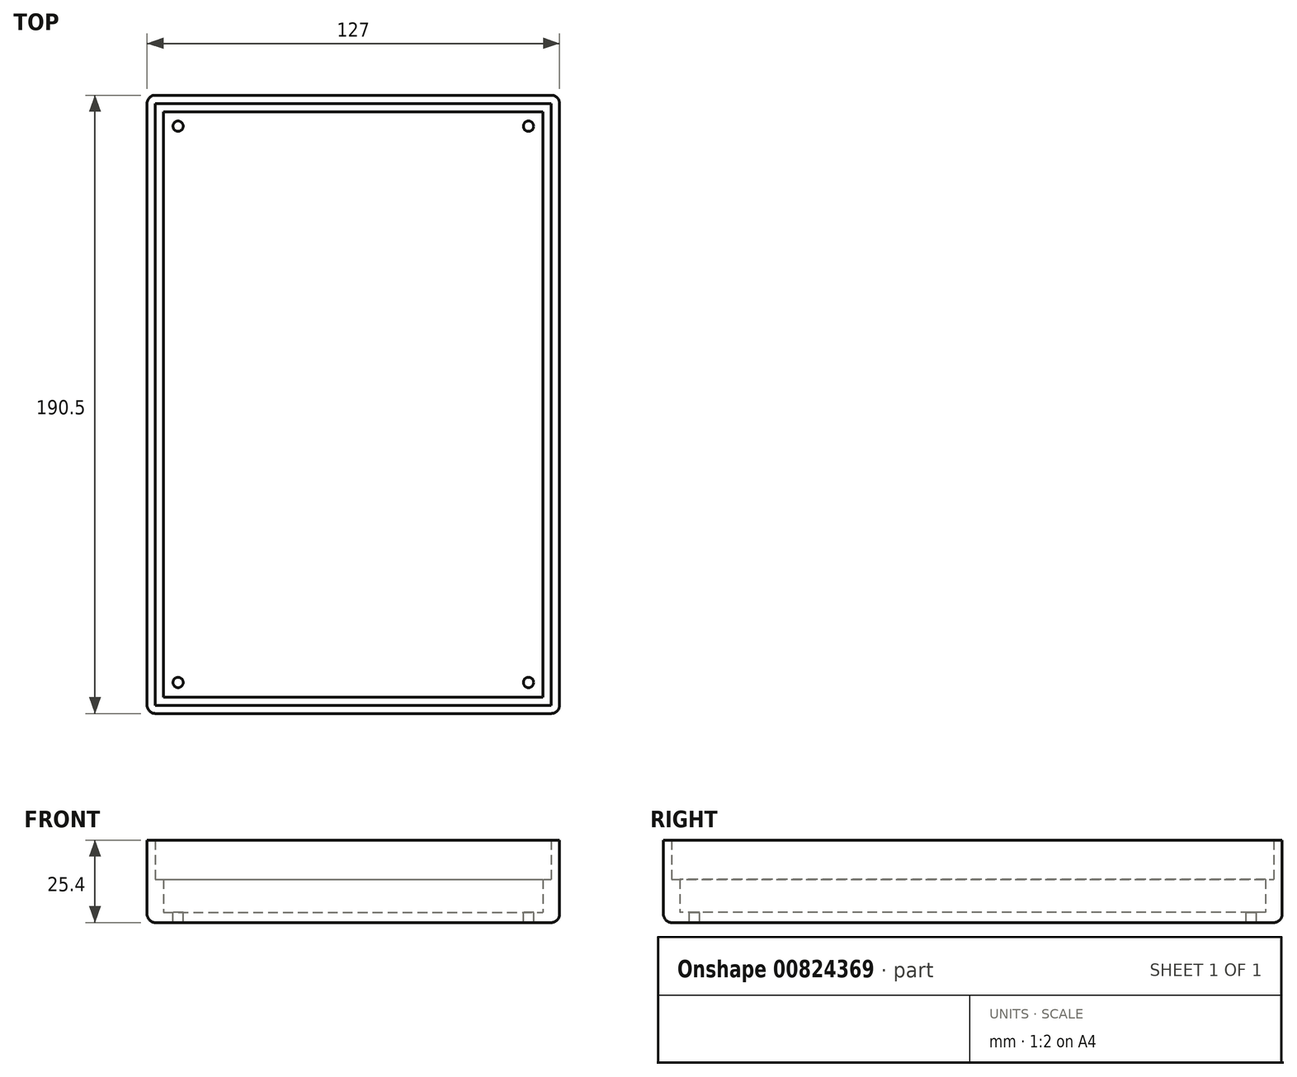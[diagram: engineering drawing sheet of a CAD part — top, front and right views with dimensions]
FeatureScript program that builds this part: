
annotation { "Feature Type Name" : "Feature", "Feature Type Description" : "" }
export const myFeature = defineFeature(function(context is Context, id is Id, definition is map)
    precondition{}
    {
        {
            var Q0;
            Q0=qCreatedBy(makeId("Top.planeOp"),FACE);
            var sketch = newSketch(context, id + "F0", { "sketchPlane" : qUnion([Q0])});
            skLineSegment(sketch, "E0.bottom", {"start": v(-60.96, 92.7) * mm, "end": v(60.96, 92.7) * mm});
            skLineSegment(sketch, "E0.top", {"start": v(-60.96, -92.7) * mm, "end": v(60.96, -92.7) * mm});
            skLineSegment(sketch, "E0.left", {"start": v(-60.96, 92.7) * mm, "end": v(-60.96, -92.7) * mm});
            skLineSegment(sketch, "E0.right", {"start": v(60.96, 92.7) * mm, "end": v(60.96, -92.7) * mm});
            skLineSegment(sketch, "E1.bottom", {"start": v(-63.5, 95.25) * mm, "end": v(63.5, 95.25) * mm});
            skLineSegment(sketch, "E1.top", {"start": v(-63.5, -95.25) * mm, "end": v(63.5, -95.25) * mm});
            skLineSegment(sketch, "E1.left", {"start": v(-63.5, 95.25) * mm, "end": v(-63.5, -95.25) * mm});
            skLineSegment(sketch, "E1.right", {"start": v(63.5, 95.25) * mm, "end": v(63.5, -95.25) * mm});
            skSolve(sketch);
        }
        {
            var Q0;
            Q0=makeQuery(id+"F0.imprint","IMPRINT",FACE,{"disambiguationData":[TD([[makeQuery(id+"F0.imprint","IMPRINT",EDGE,{"derivedFrom":sQuery(id+"F0.wireOp",EDGE,"E0.bottom")}),1.0]])]});
            extrude(context, id + "F1", {"entities" : qUnion([Q0]), "depth" : 25.4 * mm, "offsetDistance" : 25.4 * mm});
        }
        {
            var Q0;
            Q0=makeQuery(id+"F1.opExtrude","SWEPT_FACE",FACE,{"disambiguationData":[OSD([sQuery(id+"F0.wireOp",EDGE,"E0.bottom")])]});
            var sketch = newSketch(context, id + "F2", { "sketchPlane" : qUnion([Q0])});
            skLineSegment(sketch, "E2", {"start": v(-60.96, 3.18) * mm, "end": v(60.96, 3.18) * mm});
            skSolve(sketch);
        }
        {
            var Q0;
            {var subQ0=sQuery(id+"F2.wireOp",EDGE,"E2");Q0=makeQuery(id+"F2.imprint","IMPRINT",FACE,{"disambiguationData":[TD([[makeQuery(id+"F2.imprint","IMPRINT",EDGE,{"derivedFrom":subQ0}),-1.0]])]});}
            extrude(context, id + "F3", {"entities" : qUnion([Q0]), "operationType" : NewBodyOperationType.ADD, "depth" : 185.42 * mm, "offsetDistance" : 25.4 * mm});
        }
        {
            var Q0;
            Q0=makeQuery(id+"F3.opExtrude","SWEPT_FACE",FACE,{"disambiguationData":[OSD([sQuery(id+"F2.wireOp",EDGE,"E2")])]});
            var sketch = newSketch(context, id + "F4", { "sketchPlane" : qUnion([Q0])});
            skLineSegment(sketch, "E3.bottom", {"start": v(-58.42, 90.17) * mm, "end": v(58.42, 90.17) * mm});
            skLineSegment(sketch, "E3.top", {"start": v(-58.42, -90.17) * mm, "end": v(58.42, -90.17) * mm});
            skLineSegment(sketch, "E3.left", {"start": v(-58.42, 90.17) * mm, "end": v(-58.42, -90.17) * mm});
            skLineSegment(sketch, "E3.right", {"start": v(58.42, 90.17) * mm, "end": v(58.42, -90.17) * mm});
            skSolve(sketch);
        }
        {
            var Q0;
            Q0=makeQuery(id+"F4.imprint","IMPRINT",FACE,{"disambiguationData":[TD([[makeQuery(id+"F4.imprint","IMPRINT",EDGE,{"derivedFrom":sQuery(id+"F4.wireOp",EDGE,"E3.bottom")}),1.0]])]});
            extrude(context, id + "F5", {"entities" : qUnion([Q0]), "operationType" : NewBodyOperationType.ADD, "depth" : 10.16 * mm, "offsetDistance" : 25.4 * mm});
        }
        {
            var Q0;
            Q0=makeQuery(id+"F3.opExtrude","SWEPT_FACE",FACE,{"disambiguationData":[OSD([sQuery(id+"F2.wireOp",EDGE,"E2")])]});
            var sketch = newSketch(context, id + "F6", { "sketchPlane" : qUnion([Q0])});
            skLineSegment(sketch, "E4.bottom", {"start": v(-53.95, 85.7) * mm, "end": v(53.95, 85.7) * mm, "construction": true});
            skLineSegment(sketch, "E4.top", {"start": v(-53.95, -85.7) * mm, "end": v(53.95, -85.7) * mm, "construction": true});
            skLineSegment(sketch, "E4.left", {"start": v(-53.95, 85.7) * mm, "end": v(-53.95, -85.7) * mm, "construction": true});
            skLineSegment(sketch, "E4.right", {"start": v(53.95, 85.7) * mm, "end": v(53.95, -85.7) * mm, "construction": true});
            skCircle(sketch, "E5", {"center": v(-53.95, 85.7) * mm, "radius": 1.59 * mm});
            skCircle(sketch, "E6", {"center": v(53.95, 85.7) * mm, "radius": 1.59 * mm});
            skCircle(sketch, "E7", {"center": v(-53.95, -85.7) * mm, "radius": 1.59 * mm});
            skCircle(sketch, "E8", {"center": v(53.95, -85.7) * mm, "radius": 1.59 * mm});
            skSolve(sketch);
        }
        {
            var Q0;
            Q0=makeQuery(id+"F6.imprint","IMPRINT",FACE,{"disambiguationData":[TD([[makeQuery(id+"F6.imprint","IMPRINT",EDGE,{"derivedFrom":sQuery(id+"F6.wireOp",EDGE,"E5")}),1.0]])]});
            var Q1;
            Q1=makeQuery(id+"F6.imprint","IMPRINT",FACE,{"disambiguationData":[TD([[makeQuery(id+"F6.imprint","IMPRINT",EDGE,{"derivedFrom":sQuery(id+"F6.wireOp",EDGE,"E6")}),1.0]])]});
            var Q2;
            Q2=makeQuery(id+"F6.imprint","IMPRINT",FACE,{"disambiguationData":[TD([[makeQuery(id+"F6.imprint","IMPRINT",EDGE,{"derivedFrom":sQuery(id+"F6.wireOp",EDGE,"E7")}),1.0]])]});
            var Q3;
            Q3=makeQuery(id+"F6.imprint","IMPRINT",FACE,{"disambiguationData":[TD([[makeQuery(id+"F6.imprint","IMPRINT",EDGE,{"derivedFrom":sQuery(id+"F6.wireOp",EDGE,"E8")}),1.0]])]});
            extrude(context, id + "F7", {"entities" : qUnion([Q0, Q1, Q2, Q3]), "operationType" : NewBodyOperationType.REMOVE, "oppositeDirection" : true, "depth" : 25.4 * mm, "offsetDistance" : 25.4 * mm});
        }
        {
            var Q0;
            Q0=makeQuery(id+"F1.opExtrude","SWEPT_EDGE",EDGE,{"disambiguationData":[OSD([sQuery(id+"F0.wireOp",EDGE,"E1.bottom"),sQuery(id+"F0.wireOp",EDGE,"E1.left")])]});
            var Q1;
            Q1=makeQuery(id+"F1.opExtrude","CAP_EDGE",EDGE,{"disambiguationData":[OSD([sQuery(id+"F0.wireOp",EDGE,"E1.left")])],"isStart":true});
            var Q2;
            Q2=makeQuery(id+"F1.opExtrude","CAP_EDGE",EDGE,{"disambiguationData":[OSD([sQuery(id+"F0.wireOp",EDGE,"E1.bottom")])],"isStart":true});
            var Q3;
            Q3=makeQuery(id+"F1.opExtrude","SWEPT_EDGE",EDGE,{"disambiguationData":[OSD([sQuery(id+"F0.wireOp",EDGE,"E1.bottom"),sQuery(id+"F0.wireOp",EDGE,"E1.right")])]});
            var Q4;
            Q4=makeQuery(id+"F1.opExtrude","CAP_EDGE",EDGE,{"disambiguationData":[OSD([sQuery(id+"F0.wireOp",EDGE,"E1.right")])],"isStart":true});
            var Q5;
            Q5=makeQuery(id+"F1.opExtrude","CAP_EDGE",EDGE,{"disambiguationData":[OSD([sQuery(id+"F0.wireOp",EDGE,"E1.top")])],"isStart":true});
            var Q6;
            Q6=makeQuery(id+"F1.opExtrude","SWEPT_EDGE",EDGE,{"disambiguationData":[OSD([sQuery(id+"F0.wireOp",EDGE,"E1.top"),sQuery(id+"F0.wireOp",EDGE,"E1.right")])]});
            var Q7;
            Q7=makeQuery(id+"F1.opExtrude","SWEPT_EDGE",EDGE,{"disambiguationData":[OSD([sQuery(id+"F0.wireOp",EDGE,"E1.top"),sQuery(id+"F0.wireOp",EDGE,"E1.left")])]});
            fillet(context, id + "F8", {"entities" : qUnion([Q0, Q1, Q2, Q3, Q4, Q5, Q6, Q7]), "radius" : 2.54 * mm, "tangentPropagation" : true, "allowEdgeOverflow" : false});
        }
    });
